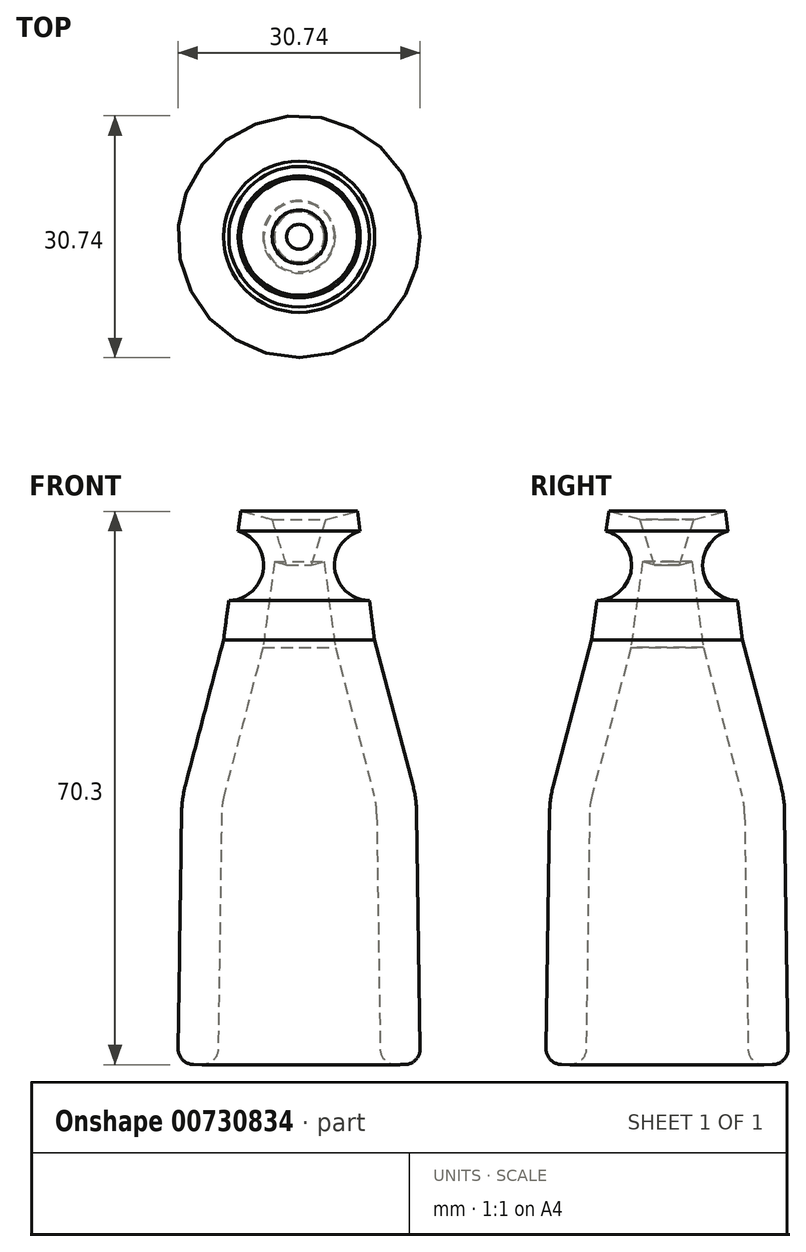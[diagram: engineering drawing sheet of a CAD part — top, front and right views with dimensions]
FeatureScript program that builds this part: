
annotation { "Feature Type Name" : "Feature", "Feature Type Description" : "" }
export const myFeature = defineFeature(function(context is Context, id is Id, definition is map)
    precondition{}
    {
        {
            var Q0;
            Q0=qCreatedBy(makeId("Front.planeOp"),FACE);
            var sketch = newSketch(context, id + "F0", { "sketchPlane" : qUnion([Q0])});
            skLineSegment(sketch, "E0", {"start": v(0, 0) * mm, "end": v(0, 63.5) * mm, "construction": true});
            skArc(sketch, "E1", {"start": v(9.85, 31.9) * mm, "mid": v(9.76, 33.08) * mm, "end": v(9.53, 34.25) * mm});
            skLineSegment(sketch, "E2", {"start": v(10.32, 0) * mm, "end": v(9.85, 31.9) * mm});
            skLineSegment(sketch, "E3", {"start": v(9.53, 34.25) * mm, "end": v(4.6, 53) * mm});
            skLineSegment(sketch, "E4", {"start": v(4.6, 53) * mm, "end": v(3.15, 63.92) * mm});
            skLineSegment(sketch, "E5", {"start": v(3.15, 63.92) * mm, "end": v(1.59, 63.5) * mm});
            skLineSegment(sketch, "E6.0", {"start": v(7.42, 70.33) * mm, "end": v(3.42, 69.25) * mm});
            skLineSegment(sketch, "E6.1", {"start": v(15.4, 0.07) * mm, "end": v(14.93, 31.97) * mm});
            skArc(sketch, "E6.2", {"start": v(14.93, 31.97) * mm, "mid": v(14.8, 33.77) * mm, "end": v(14.44, 35.54) * mm});
            skLineSegment(sketch, "E6.3", {"start": v(14.44, 35.54) * mm, "end": v(9.6, 53.99) * mm});
            skLineSegment(sketch, "E6.4", {"start": v(9.6, 53.99) * mm, "end": v(7.42, 70.33) * mm});
            skLineSegment(sketch, "E7", {"start": v(3.42, 69.25) * mm, "end": v(1.59, 63.5) * mm});
            skLineSegment(sketch, "E8", {"start": v(15.4, 0.07) * mm, "end": v(10.32, 0) * mm});
            skLineSegment(sketch, "E9", {"start": v(-8.79, 63.5) * mm, "end": v(9, 63.5) * mm, "construction": true});
            skCircle(sketch, "E10", {"center": v(9, 63.5) * mm, "radius": 4.5 * mm});
            skSolve(sketch);
        }
        {
            var Q0;
            Q0=qCreatedBy(makeId("Front.planeOp"),FACE);
            var sketch = newSketch(context, id + "F1", { "sketchPlane" : qUnion([Q0])});
            skLineSegment(sketch, "E11", {"start": v(0, 0) * mm, "end": v(0, 84.81) * mm, "construction": true});
            skSolve(sketch);
        }
        {
            var Q0;
            Q0=makeQuery(id+"F0.imprint","IMPRINT",FACE,{"disambiguationData":[TD([[makeQuery(id+"F0.imprint","IMPRINT",EDGE,{"derivedFrom":sQuery(id+"F0.wireOp",EDGE,"E1")}),-1.0]])]});
            var Q1;
            Q1=sQuery(id+"F1.wireOp",EDGE,"E11");
            revolve(context, id + "F2", {"surfaceOperationType" : NewSurfaceOperationType.NEW, "entities" : qUnion([Q0]), "axis" : qUnion([Q1]), "revolveType" : RevolveType.FULL});
        }
        {
            var Q0;
            Q0=makeQuery(id+"F2.opRevolve","SWEPT_EDGE",EDGE,{"disambiguationData":[OSD([sQuery(id+"F0.wireOp",EDGE,"E6.1"),sQuery(id+"F0.wireOp",EDGE,"E8")])]});
            var Q1;
            Q1=makeQuery(id+"F2.opRevolve","SWEPT_EDGE",EDGE,{"disambiguationData":[OSD([sQuery(id+"F0.wireOp",EDGE,"E2"),sQuery(id+"F0.wireOp",EDGE,"E8")])]});
            fillet(context, id + "F3", {"entities" : qUnion([Q0, Q1]), "radius" : 2 * mm, "tangentPropagation" : true, "allowEdgeOverflow" : false});
        }
    });
